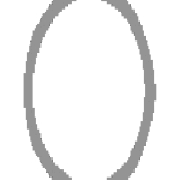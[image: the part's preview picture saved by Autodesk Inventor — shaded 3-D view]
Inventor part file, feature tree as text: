
AUTODESK INVENTOR PART (.ipt)
format: ipt  version: 2021 (Build 250183000, 183)  size: 112,640 bytes
history: native  units: in
note: dims shown in document units (in); Inventor stores cm internally (conversion verified against a paired STEP export)
features: other x4, sketch x3, plane x1
ambient origin geometry x8: Origin, YZ Plane, XZ Plane, XY Plane, X Axis, Y Axis, Z Axis, Center Point
bodies: Solid1 (feature_tree), Body (feature_tree)
feature tree (8):
  other  "Driven Length"
  other  "Frame Generator"
  other  "Start Plane"
  other  "End Plane"
  sketch  "Sketch"  dims[d2=28.9in d4=-0.0in d5=28.9in d6=0.12in d7=0.0in d8=90.0deg d9=28.9in]
  sketch  "Sketch2"  dims[d0=1.0in]
  plane  "Work Plane3"
  sketch  "Sketch3"  dims[d1=0.065in]
